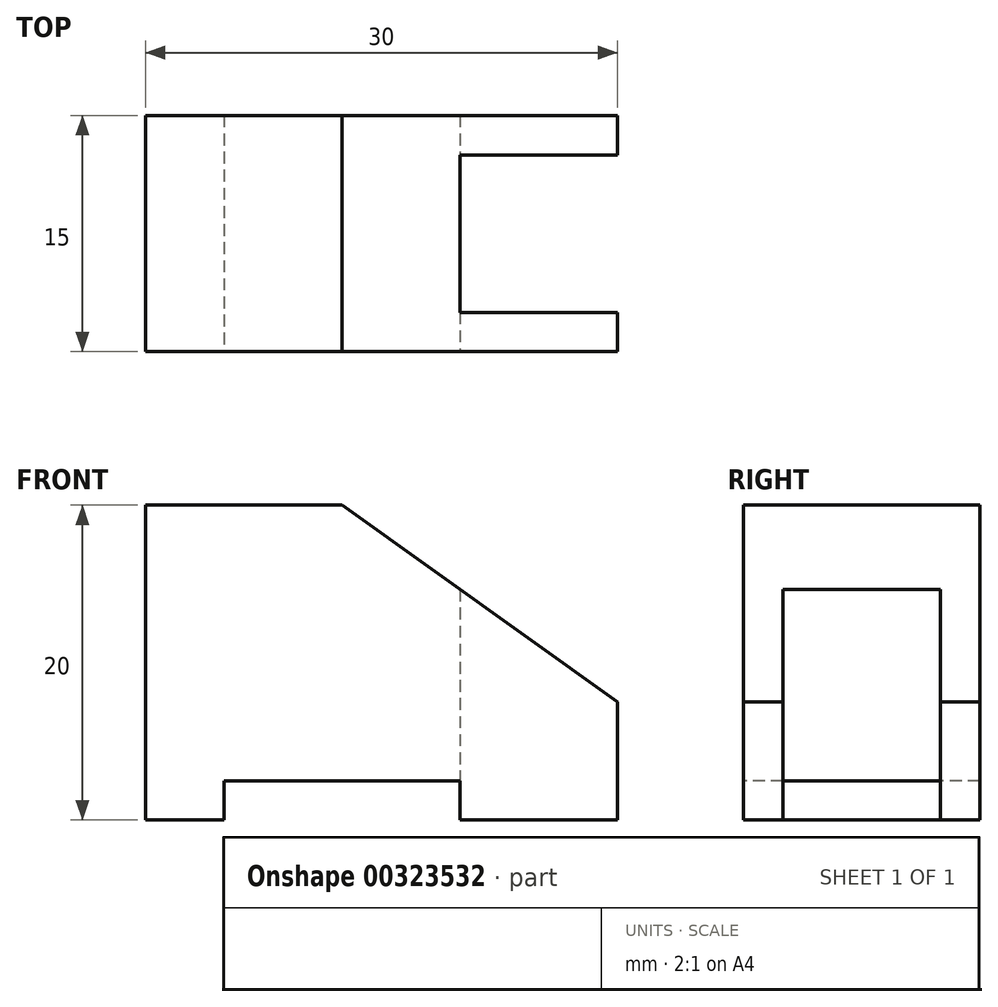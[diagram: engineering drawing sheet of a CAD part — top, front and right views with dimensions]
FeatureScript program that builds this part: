
annotation { "Feature Type Name" : "Feature", "Feature Type Description" : "" }
export const myFeature = defineFeature(function(context is Context, id is Id, definition is map)
    precondition{}
    {
        {
            var Q0;
            Q0=qCreatedBy(makeId("Top.planeOp"),FACE);
            var sketch = newSketch(context, id + "F0", { "sketchPlane" : qUnion([Q0])});
            skLineSegment(sketch, "E0.bottom", {"start": v(0, 0) * mm, "end": v(30, 0) * mm});
            skLineSegment(sketch, "E0.top", {"start": v(0, 15) * mm, "end": v(30, 15) * mm});
            skLineSegment(sketch, "E0.left", {"start": v(0, 0) * mm, "end": v(0, 15) * mm});
            skLineSegment(sketch, "E1", {"start": v(30, 15) * mm, "end": v(30, 12.5) * mm});
            skLineSegment(sketch, "E2", {"start": v(30, 12.5) * mm, "end": v(20, 12.5) * mm});
            skLineSegment(sketch, "E3", {"start": v(20, 12.5) * mm, "end": v(20, 2.5) * mm});
            skLineSegment(sketch, "E4", {"start": v(20, 2.5) * mm, "end": v(30, 2.5) * mm});
            skLineSegment(sketch, "E5", {"start": v(30, 2.5) * mm, "end": v(30, 0) * mm});
            skSolve(sketch);
        }
        {
            var Q0;
            Q0 = qSketchRegion(id + "F0", true);
            extrude(context, id + "F1", {"entities" : qUnion([Q0]), "depth" : 20 * mm});
        }
        {
            var Q0;
            Q0=makeQuery(id+"F1.opExtrude","SWEPT_FACE",FACE,{"disambiguationData":[OSD([sQuery(id+"F0.wireOp",EDGE,"E0.bottom")])]});
            var sketch = newSketch(context, id + "F2", { "sketchPlane" : qUnion([Q0])});
            skLineSegment(sketch, "E6", {"start": v(30, 20) * mm, "end": v(30, 7.5) * mm});
            skLineSegment(sketch, "E7", {"start": v(30, 7.5) * mm, "end": v(12.5, 20) * mm});
            skLineSegment(sketch, "E8", {"start": v(12.5, 20) * mm, "end": v(30, 20) * mm});
            skSolve(sketch);
        }
        {
            var Q0;
            Q0 = qSketchRegion(id + "F2", true);
            extrude(context, id + "F3", {"entities" : qUnion([Q0]), "operationType" : NewBodyOperationType.REMOVE, "oppositeDirection" : true, "depth" : 25 * mm});
        }
        {
            var Q0;
            Q0=makeQuery(id+"F1.opExtrude","SWEPT_FACE",FACE,{"disambiguationData":[OSD([sQuery(id+"F0.wireOp",EDGE,"E0.bottom")])]});
            var sketch = newSketch(context, id + "F4", { "sketchPlane" : qUnion([Q0])});
            skLineSegment(sketch, "E9.bottom", {"start": v(5, 0) * mm, "end": v(20, 0) * mm});
            skLineSegment(sketch, "E9.top", {"start": v(5, 2.5) * mm, "end": v(20, 2.5) * mm});
            skLineSegment(sketch, "E9.left", {"start": v(5, 0) * mm, "end": v(5, 2.5) * mm});
            skLineSegment(sketch, "E9.right", {"start": v(20, 0) * mm, "end": v(20, 2.5) * mm});
            skSolve(sketch);
        }
        {
            var Q0;
            Q0 = qSketchRegion(id + "F4", true);
            extrude(context, id + "F5", {"entities" : qUnion([Q0]), "operationType" : NewBodyOperationType.REMOVE, "oppositeDirection" : true, "depth" : 25 * mm});
        }
    });
